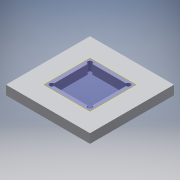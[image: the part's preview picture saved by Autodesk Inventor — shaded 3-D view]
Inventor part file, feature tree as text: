
AUTODESK INVENTOR PART (.ipt)
format: ipt  version: 2017 (Build 210142000, 142)  size: 156,672 bytes
history: native  units: mm
features: sketch x7, hole x4, extrude x3, projected_geometry x3, other x1, split x1
ambient origin geometry x8: Origin, YZ Plane, XZ Plane, XY Plane, X Axis, Y Axis, Z Axis, Center Point
bodies: Body1 (feature_tree)
feature tree (19):
  extrude  "Extrusion1"  Depth=55.0mm
  hole  "Hole2"  [1 undecoded]
  extrude  "Extrusion3"  Depth=6.0mm TaperAngle=0.0deg
  hole  "Hole3"  [1 undecoded]
  extrude  "Extrusion4"  Depth=25.0mm
  hole  "Hole5"  [1 undecoded]
  hole  "Hole6"  [1 undecoded]
  other  "SplitPlane"
  split  "Split3"
  sketch  "Sketch1"  dims[d0=55.0mm d1=55.0mm]
  sketch  "Sketch4"  dims[d2=20.0mm d3=0.0mm d15=45.1mm]
  sketch  "Sketch5"  dims[d16=45.1mm]
  sketch  "Sketch6"  dims[d17=5.0mm d18=6.0mm d19=4.0mm d20=2.0mm d21=90.0deg d22=8.0mm d23=0.0mm d24=8.0mm d25=0.0mm]
  projected_geometry  "Projected Loop1"
  sketch  "Sketch8"  dims[d26=15.0mm d27=15.0mm]
  projected_geometry  "Projected Loop2"
  sketch  "Sketch9"  dims[d28=3.242mm d29=6.0mm d30=4.0mm d31=2.0mm d32=90.0deg d33=8.0mm d34=20.594885mm d44=25.0mm]
  projected_geometry  "Projected Loop3"
  sketch  "Sketch10"  dims[d45=25.0mm d46=6.0mm d47=0.0mm d48=3.0mm d49=6.0mm d50=4.0mm d51=2.0mm d52=90.0deg d53=6.0mm d54=0.0mm d55=3.242mm d56=8.0mm d57=4.0mm d58=2.0mm d59=90.0deg d60=4.0mm d61=20.594885mm d62=0.0mm]
note: 4 required parameter values undecoded (feature->parameter linkage not recoverable at this tier; creation-order binding heuristic only, values carry confidence <= 0.55)
